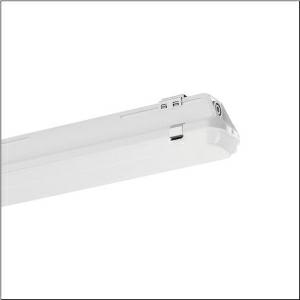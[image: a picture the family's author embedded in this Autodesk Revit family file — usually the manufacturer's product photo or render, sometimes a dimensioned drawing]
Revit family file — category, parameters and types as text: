
# Revit family: monsun_r__12_emergency_51fp20dp467h3h_9710
name_source: partatom
category: Lighting Fixtures
units: mm (PartAtom-declared; Revit-internal decimal feet)

## family parameters
Cut with Voids When Loaded = No
Host = Face
Light Source = No
Part Type = Normal
Room Calculation Point = No
Round Connector Dimension = Use Diameter
Shared = No

## types (1)
- --- (1 x LED, 790 lm, 5 W, 4000K)
    Apparent Load = 5 VA
    CIE Flux Codes = 45 75 93 94 100
    Color Rendering = 80
    Color Temperature = 4000K
    Default Elevation = 1800 mm
    Description = Monsun® 12 emergency, damp-proof luminaire, chain hanger, primary optical cover: enclosure, of PC, light emission: direct distribution, primary light characteristic: symmetric, installation type: suspended mounting, surface-mounted, horizontal mounting, vertical mounting, LED rated luminous flux: 5.450 lm, light colour: 840, colour temperature: 4000K, control gear: ECG DALI, with terminal, 5+3-pole, max. 2.5mm², mains connection: 220..240V, AC, 50/60Hz, rated input power: 35W, control gear: single battery element, battery: NiCd, 4,5 Ah, mains connection: 230V, luminaire housing, of glass-fibre reinforced polyester, uncoated, bright grey, length: 1.590 mm, width: 90 mm, height: 88mm, clip for enclosure, of stainless steel (V2A), ceiling mounting element, of stainless steel (V2A), chain hanger, of stainless steel (V2A), protection rating (complete): IP66, insulation class (complete): insulation class I (protective earthing), certification: CE, protection symbol: D, impact resistance: IK08, permissible ambient temperature for indoor applications: +5..+35°C, standard: EN 50419, EN 60598-2-1, EN 60598-2-22, no direct snow, no direct sun, no direct rain, for indoor or canopied outdoor use, corresponds to IFS (International Featured Standards) requirements for safety and quality in the food industry, packaging unit: 1 piece
    Height = 89 mm
    Lamp = 1 x LED
    Lamp Light Flux = 790 lm
    Lamp Power = 5 W
    Lamp count = 1
    Length = 1590 mm
    Luminous efficacy = 158 lm/W
    Manufacturer = Siteco
    ModVariant = No
    Model = 51FP20DP467H3H
    Mounting Place = Ceiling
    Mounting Type = Pendant
    Number of Poles = 1
    OnlyDefault = Yes
    Power Factor = 1
    Product Name = Monsun® 12 emergency
    Product group = damp-proof luminaire | ceiling pendant
    ProductGroupID = 908
    Protection Class = Protection class I
    Protection Degree = IP 66
    RLX_Detail_Level = 1
    RlxData = <blob elided: 92049 chars, md5=aac7ed50>
    Socket = socket
    Standby Power = 0 W
    System Light Flux = 790 lm
    System Power = 5 W
    Type Comments = : emergency light operation: 3 h
    Type Image = l_1004748.jpg
    URL = http://relux.com
    VarID = @adj_125631
    Voltage = 0 V
    Weight = 0.00 kg
    Width = 90 mm

## geometry (parser evidence)
native form markers: Blend x4, Sweep x13
no freeform markers — native parametric forms only
